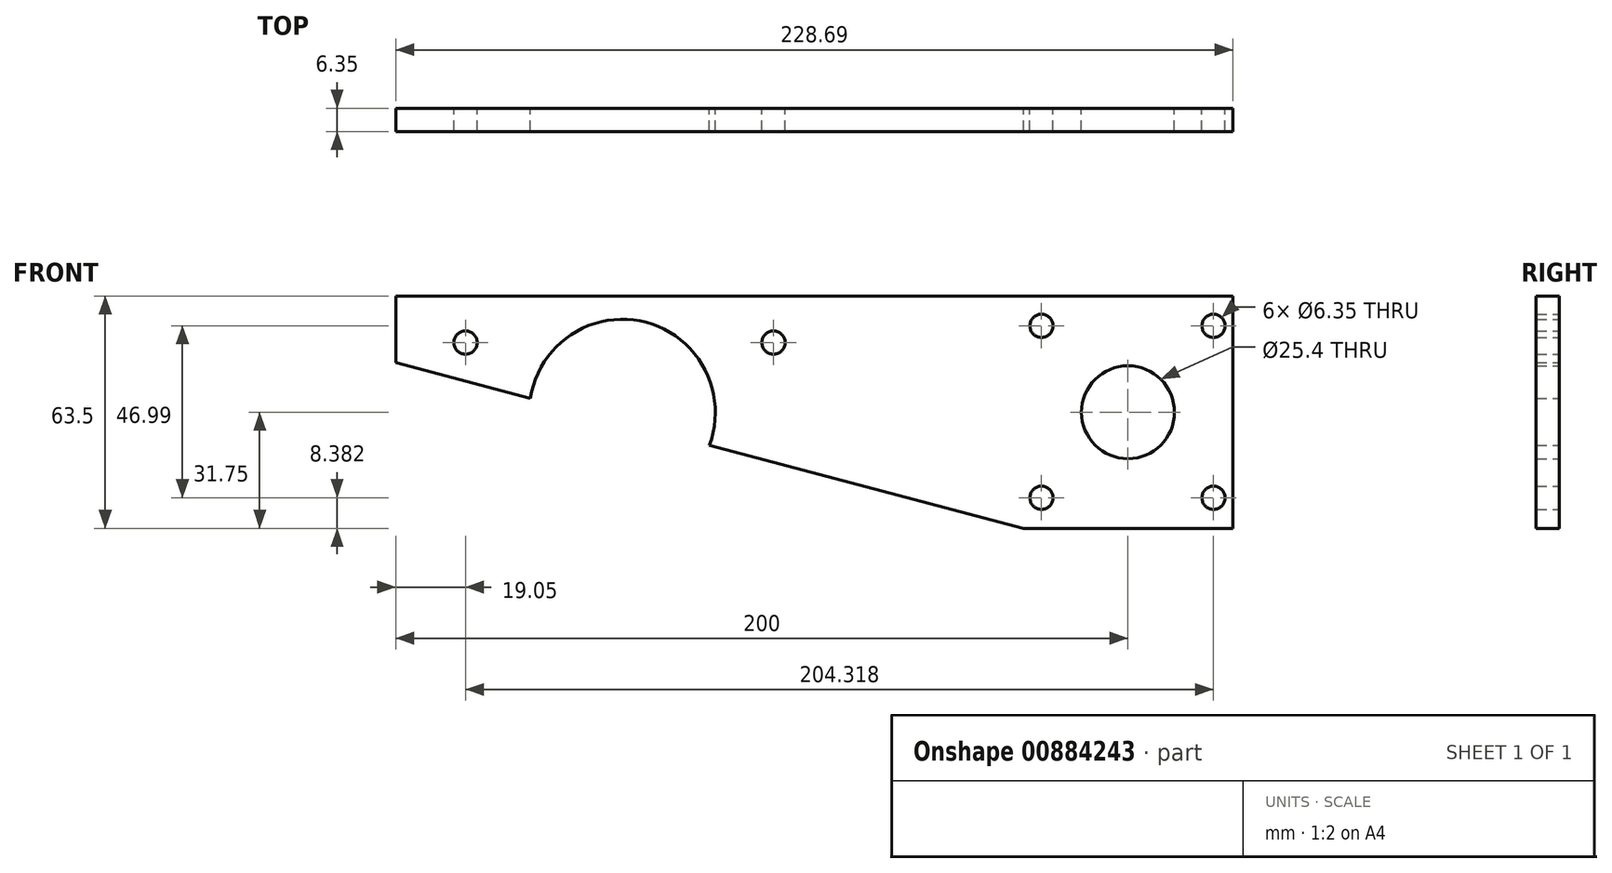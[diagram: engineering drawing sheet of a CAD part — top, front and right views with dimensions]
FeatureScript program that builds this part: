
annotation { "Feature Type Name" : "Feature", "Feature Type Description" : "" }
export const myFeature = defineFeature(function(context is Context, id is Id, definition is map)
    precondition{}
    {
        {
            var Q0;
            Q0=qCreatedBy(makeId("Front.planeOp"),FACE);
            var sketch = newSketch(context, id + "F0", { "sketchPlane" : qUnion([Q0])});
            skCircle(sketch, "E0", {"center": v(41.27, 19.05) * mm, "radius": 3.18 * mm});
            skCircle(sketch, "E1", {"center": v(-42.85, 19.05) * mm, "radius": 3.18 * mm});
            skCircle(sketch, "E2", {"center": v(138.1, 0) * mm, "radius": 12.7 * mm});
            skCircle(sketch, "E3", {"center": v(161.47, 23.62) * mm, "radius": 3.18 * mm});
            skCircle(sketch, "E4", {"center": v(114.48, 23.62) * mm, "radius": 3.18 * mm});
            skCircle(sketch, "E5", {"center": v(114.48, -23.37) * mm, "radius": 3.18 * mm});
            skCircle(sketch, "E6", {"center": v(161.47, -23.37) * mm, "radius": 3.18 * mm});
            skLineSegment(sketch, "E7.bottom", {"start": v(-61.9, 31.75) * mm, "end": v(166.79, 31.75) * mm});
            skLineSegment(sketch, "E7.top", {"start": v(109.64, -31.75) * mm, "end": v(166.79, -31.75) * mm});
            skLineSegment(sketch, "E7.left", {"start": v(-61.9, 31.75) * mm, "end": v(-61.9, 13.57) * mm});
            skLineSegment(sketch, "E7.right", {"start": v(166.79, 31.75) * mm, "end": v(166.79, -31.75) * mm});
            skLineSegment(sketch, "E8", {"start": v(-61.9, 13.57) * mm, "end": v(-25.1, 3.85) * mm});
            skArc(sketch, "E9", {"start": v(23.73, -9.05) * mm, "mid": v(6.49, 24.56) * mm, "end": v(-25.1, 3.85) * mm});
            skLineSegment(sketch, "E10.trimOffspring", {"start": v(23.73, -9.05) * mm, "end": v(109.64, -31.75) * mm});
            skSolve(sketch);
        }
        {
            var Q0;
            Q0 = qSketchRegion(id + "F0", true);
            extrude(context, id + "F1", {"entities" : qUnion([Q0]), "depth" : 6.35 * mm, "offsetDistance" : 25.4 * mm});
        }
    });
